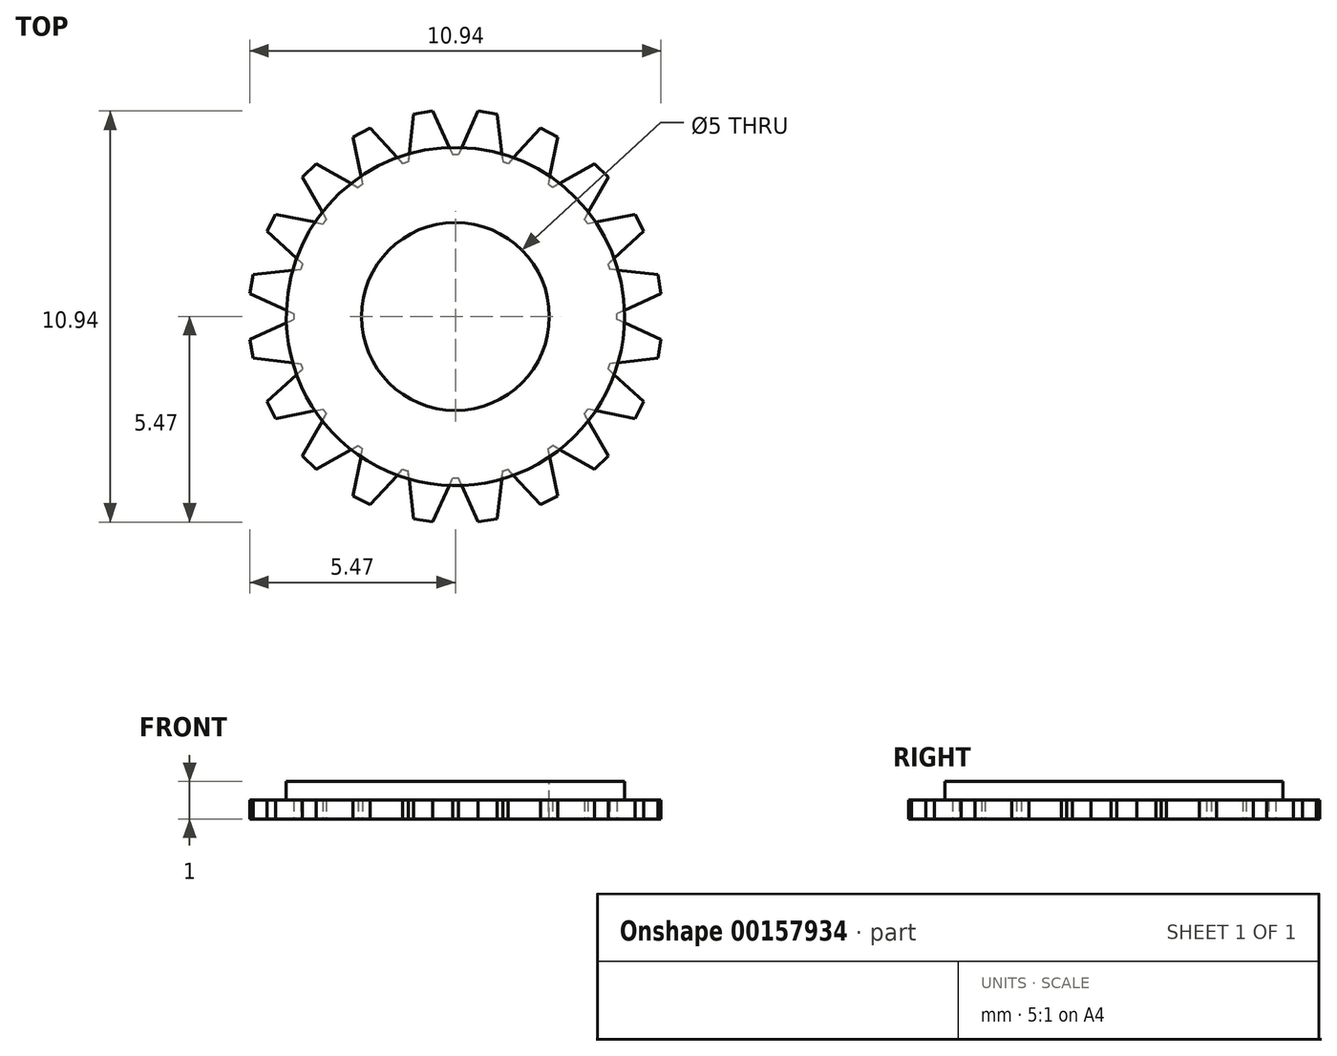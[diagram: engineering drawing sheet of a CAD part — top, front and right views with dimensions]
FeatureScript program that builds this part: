
annotation { "Feature Type Name" : "Feature", "Feature Type Description" : "" }
export const myFeature = defineFeature(function(context is Context, id is Id, definition is map)
    precondition{}
    {
        {
            var Q0;
            Q0=qCreatedBy(makeId("Front.planeOp"),FACE);
            var sketch = newSketch(context, id + "F0", { "sketchPlane" : qUnion([Q0])});
            skLineSegment(sketch, "E0", {"start": v(0, 0) * mm, "end": v(0, 40.99) * mm, "construction": true});
            skSolve(sketch);
        }
        {
            assignVariable(context, id + "F1", {"name" : "config", "anyValue" : 0});
        }
        {
            assignVariable(context, id + "F2", {"name" : "H1", "anyValue" : [0.5, 0.15][getVariable(context, 'config')]});
        }
        {
            assignVariable(context, id + "F3", {"name" : "H3", "anyValue" : [0.5, 0.02][getVariable(context, 'config')]});
        }
        {
            assignVariable(context, id + "F4", {"name" : "N1", "anyValue" : [20, 40][getVariable(context, 'config')]});
        }
        {
            var Q0;
            Q0=qCreatedBy(makeId("Top.planeOp"),FACE);
            var sketch = newSketch(context, id + "F5", { "sketchPlane" : qUnion([Q0])});
            skCircle(sketch, "E1", {"center": v(0, 0) * mm, "radius": 5.5 * mm, "construction": true});
            skCircle(sketch, "E2", {"center": v(0, 0) * mm, "radius": 4.3 * mm});
            skCircle(sketch, "E3", {"center": v(0, 0) * mm, "radius": 5 * mm, "construction": true});
            skLineSegment(sketch, "E4", {"start": v(0, 0) * mm, "end": v(0, 4.3) * mm});
            skLineSegment(sketch, "E5", {"start": v(0, 0) * mm, "end": v(1.33, 4.09) * mm});
            skLineSegment(sketch, "E6", {"start": v(0.86, 5.43) * mm, "end": v(0, 0) * mm, "construction": true});
            skLineSegment(sketch, "E7", {"start": v(0.4, 5) * mm, "end": v(1.17, 4.88) * mm, "construction": true});
            skPoint(sketch, "E8", {"position": v(0.78, 4.94) * mm});
            skLineSegment(sketch, "E9", {"start": v(0, 0) * mm, "end": v(0.43, 5.48) * mm, "construction": true});
            skLineSegment(sketch, "E10", {"start": v(0.6, 5.47) * mm, "end": v(0.08, 4.3) * mm});
            skLineSegment(sketch, "E11.MirrorCS", {"start": v(1.11, 5.39) * mm, "end": v(1.26, 4.11) * mm});
            skLineSegment(sketch, "E12", {"start": v(0.6, 5.47) * mm, "end": v(1.11, 5.39) * mm});
            skLineSegment(sketch, "E13", {"start": v(-2.33, 5.2) * mm, "end": v(4.02, 4.7) * mm, "construction": true});
            skPoint(sketch, "E14", {"position": v(0.39, 4.98) * mm});
            skLineSegment(sketch, "E15", {"start": v(0.39, 4.98) * mm, "end": v(-0.1, 5.2) * mm, "construction": true});
            skSolve(sketch);
        }
        {
            var Q0;
            {var subQ0=sQuery(id+"F5.wireOp",EDGE,"E10");Q0=makeQuery(id+"F5.imprint","IMPRINT",FACE,{"disambiguationData":[TD([[makeQuery(id+"F5.imprint","IMPRINT",EDGE,{"derivedFrom":subQ0}),1.0]])]});}
            var Q1;
            {var subQ0=sQuery(id+"F5.wireOp",EDGE,"E4");Q1=makeQuery(id+"F5.imprint","IMPRINT",FACE,{"disambiguationData":[TD([[makeQuery(id+"F5.imprint","IMPRINT",EDGE,{"derivedFrom":subQ0}),-1.0]])]});}
            extrude(context, id + "F6", {"entities" : qUnion([Q0, Q1]), "depth" : (getVariable(context, 'H1')) * mm});
        }
        {
            var Q0;
            Q0=makeQuery(id+"F6.opExtrude","SWEPT_BODY",BODY,{"disambiguationData":[OSD([sQuery(id+"F5.wireOp",EDGE,"E2"),sQuery(id+"F5.wireOp",EDGE,"E4"),sQuery(id+"F5.wireOp",EDGE,"E5"),sQuery(id+"F5.wireOp",EDGE,"E10"),sQuery(id+"F5.wireOp",EDGE,"E11.MirrorCS"),sQuery(id+"F5.wireOp",EDGE,"E12")])]});
            var Q1;
            Q1=sQuery(id+"F0.wireOp",EDGE,"E0");
            circularPattern(context, id + "F7", {"operationType" : NewBodyOperationType.ADD, "entities" : qUnion([Q0]), "axis" : qUnion([Q1]), "angle" : 360 * degree, "instanceCount" : getVariable(context, 'N1'), "equalSpace" : true});
        }
        {
            var Q0;
            Q0=qCreatedBy(makeId("Top.planeOp"),FACE);
            var sketch = newSketch(context, id + "F8", { "sketchPlane" : qUnion([Q0])});
            skCircle(sketch, "E16", {"center": v(0, 0) * mm, "radius": 2.5 * mm});
            skCircle(sketch, "E17", {"center": v(0, 0) * mm, "radius": 4.5 * mm});
            skSolve(sketch);
        }
        {
            var Q0;
            {var subQ0=makeQuery(id+"F6.opExtrude","CAP_FACE",FACE,{"disambiguationData":[OSD([sQuery(id+"F5.wireOp",EDGE,"E2"),sQuery(id+"F5.wireOp",EDGE,"E4"),sQuery(id+"F5.wireOp",EDGE,"E5"),sQuery(id+"F5.wireOp",EDGE,"E10"),sQuery(id+"F5.wireOp",EDGE,"E11.MirrorCS"),sQuery(id+"F5.wireOp",EDGE,"E12")])],"isStart":false});Q0=makeQuery(id+"F7.boolean.opBoolean","MERGE",FACE,{"derivedFrom":[subQ0,makeQuery(id+"F7.opPattern","COPY",FACE,{"derivedFrom":subQ0,"instanceName":"1"}),makeQuery(id+"F7.opPattern","COPY",FACE,{"derivedFrom":subQ0,"instanceName":"2"}),makeQuery(id+"F7.opPattern","COPY",FACE,{"derivedFrom":subQ0,"instanceName":"3"}),makeQuery(id+"F7.opPattern","COPY",FACE,{"derivedFrom":subQ0,"instanceName":"4"}),makeQuery(id+"F7.opPattern","COPY",FACE,{"derivedFrom":subQ0,"instanceName":"5"}),makeQuery(id+"F7.opPattern","COPY",FACE,{"derivedFrom":subQ0,"instanceName":"6"}),makeQuery(id+"F7.opPattern","COPY",FACE,{"derivedFrom":subQ0,"instanceName":"7"}),makeQuery(id+"F7.opPattern","COPY",FACE,{"derivedFrom":subQ0,"instanceName":"8"}),makeQuery(id+"F7.opPattern","COPY",FACE,{"derivedFrom":subQ0,"instanceName":"9"}),makeQuery(id+"F7.opPattern","COPY",FACE,{"derivedFrom":subQ0,"instanceName":"10"}),makeQuery(id+"F7.opPattern","COPY",FACE,{"derivedFrom":subQ0,"instanceName":"11"}),makeQuery(id+"F7.opPattern","COPY",FACE,{"derivedFrom":subQ0,"instanceName":"12"}),makeQuery(id+"F7.opPattern","COPY",FACE,{"derivedFrom":subQ0,"instanceName":"13"}),makeQuery(id+"F7.opPattern","COPY",FACE,{"derivedFrom":subQ0,"instanceName":"14"}),makeQuery(id+"F7.opPattern","COPY",FACE,{"derivedFrom":subQ0,"instanceName":"15"}),makeQuery(id+"F7.opPattern","COPY",FACE,{"derivedFrom":subQ0,"instanceName":"16"}),makeQuery(id+"F7.opPattern","COPY",FACE,{"derivedFrom":subQ0,"instanceName":"17"}),makeQuery(id+"F7.opPattern","COPY",FACE,{"derivedFrom":subQ0,"instanceName":"18"}),makeQuery(id+"F7.opPattern","COPY",FACE,{"derivedFrom":subQ0,"instanceName":"19"}),makeQuery(id+"F7.opPattern","COPY",FACE,{"derivedFrom":subQ0,"instanceName":"20"}),makeQuery(id+"F7.opPattern","COPY",FACE,{"derivedFrom":subQ0,"instanceName":"21"}),makeQuery(id+"F7.opPattern","COPY",FACE,{"derivedFrom":subQ0,"instanceName":"22"}),makeQuery(id+"F7.opPattern","COPY",FACE,{"derivedFrom":subQ0,"instanceName":"23"}),makeQuery(id+"F7.opPattern","COPY",FACE,{"derivedFrom":subQ0,"instanceName":"24"}),makeQuery(id+"F7.opPattern","COPY",FACE,{"derivedFrom":subQ0,"instanceName":"25"}),makeQuery(id+"F7.opPattern","COPY",FACE,{"derivedFrom":subQ0,"instanceName":"26"}),makeQuery(id+"F7.opPattern","COPY",FACE,{"derivedFrom":subQ0,"instanceName":"27"}),makeQuery(id+"F7.opPattern","COPY",FACE,{"derivedFrom":subQ0,"instanceName":"28"}),makeQuery(id+"F7.opPattern","COPY",FACE,{"derivedFrom":subQ0,"instanceName":"29"}),makeQuery(id+"F7.opPattern","COPY",FACE,{"derivedFrom":subQ0,"instanceName":"30"}),makeQuery(id+"F7.opPattern","COPY",FACE,{"derivedFrom":subQ0,"instanceName":"31"}),makeQuery(id+"F7.opPattern","COPY",FACE,{"derivedFrom":subQ0,"instanceName":"32"}),makeQuery(id+"F7.opPattern","COPY",FACE,{"derivedFrom":subQ0,"instanceName":"33"}),makeQuery(id+"F7.opPattern","COPY",FACE,{"derivedFrom":subQ0,"instanceName":"34"}),makeQuery(id+"F7.opPattern","COPY",FACE,{"derivedFrom":subQ0,"instanceName":"35"}),makeQuery(id+"F7.opPattern","COPY",FACE,{"derivedFrom":subQ0,"instanceName":"36"}),makeQuery(id+"F7.opPattern","COPY",FACE,{"derivedFrom":subQ0,"instanceName":"37"}),makeQuery(id+"F7.opPattern","COPY",FACE,{"derivedFrom":subQ0,"instanceName":"38"}),makeQuery(id+"F7.opPattern","COPY",FACE,{"derivedFrom":subQ0,"instanceName":"39"}),makeQuery(id+"F7.opPattern","COPY",FACE,{"derivedFrom":subQ0,"instanceName":"40"}),makeQuery(id+"F7.opPattern","COPY",FACE,{"derivedFrom":subQ0,"instanceName":"41"}),makeQuery(id+"F7.opPattern","COPY",FACE,{"derivedFrom":subQ0,"instanceName":"42"}),makeQuery(id+"F7.opPattern","COPY",FACE,{"derivedFrom":subQ0,"instanceName":"43"}),makeQuery(id+"F7.opPattern","COPY",FACE,{"derivedFrom":subQ0,"instanceName":"44"}),makeQuery(id+"F7.opPattern","COPY",FACE,{"derivedFrom":subQ0,"instanceName":"45"}),makeQuery(id+"F7.opPattern","COPY",FACE,{"derivedFrom":subQ0,"instanceName":"46"}),makeQuery(id+"F7.opPattern","COPY",FACE,{"derivedFrom":subQ0,"instanceName":"47"}),makeQuery(id+"F7.opPattern","COPY",FACE,{"derivedFrom":subQ0,"instanceName":"48"}),makeQuery(id+"F7.opPattern","COPY",FACE,{"derivedFrom":subQ0,"instanceName":"49"})]});}
            var sketch = newSketch(context, id + "F9", { "sketchPlane" : qUnion([Q0])});
            skCircle(sketch, "E18.0", {"center": v(0, 0) * mm, "radius": 4.5 * mm});
            skSolve(sketch);
        }
        {
            var Q0;
            Q0=qSketchRegion(id+"F9",true);
            extrude(context, id + "F10", {"entities" : qUnion([Q0]), "operationType" : NewBodyOperationType.ADD, "depth" : (getVariable(context, 'H3')) * mm});
        }
        {
            var Q0;
            Q0=makeQuery(id+"F8.imprint","IMPRINT",FACE,{"disambiguationData":[TD([[makeQuery(id+"F8.imprint","IMPRINT",EDGE,{"derivedFrom":sQuery(id+"F8.wireOp",EDGE,"E16")}),1.0]])]});
            extrude(context, id + "F11", {"entities" : qUnion([Q0]), "operationType" : NewBodyOperationType.REMOVE, "endBound" : BoundingType.THROUGH_ALL, "oppositeDirection" : true, "depth" : 25 * mm, "hasSecondDirection" : true, "secondDirectionBound" : SecondDirectionBoundingType.THROUGH_ALL, "secondDirectionOppositeDirection" : false, "secondDirectionDepth" : 25 * mm});
        }
    });
